# Revit family: Kabelleiter- LG630 VS 3 FS, FT, FT SO
name_source: partatom
category: Generic Models
revit_build: Autodesk Revit 2017 (Build: 20190508_0315(x64)
units: mm (PartAtom-declared; Revit-internal decimal feet)

## family parameters
Always vertical = Yes
Can host rebar = No
Cut with Voids When Loaded = No
Part Type = Normal
Room Calculation Point = No
Round Connector Dimension = Use Diameter
Shared = No
Work Plane-Based = No

## types (3) — shared parameters
Cut's number = 40
Cut's number 2 = 10
Cut's space = 75 mm
Cut's space 2 = 300 mm
Height = 60 mm  [stored 0.19685 ft]
Length = 3000 mm  [stored 9.84252 ft]
Manufacturer = OBO Bettermann
URL = http://obo-bettermann.com
Width = 300 mm
Width/2 = 150 mm

## per-type parameters (varying)
| type | GTIN | Manufacturer Art.No. | Material |
| LG 630 VS 3 FS | 4012195064053 | 6208541 | Strip-galvanised |
| LG 630 VS 3 FT | 4012195434160 | 6208566 | Hot-dip galvanised |
| LG 630 VS 3FT SO | 4012195363279 | 7186361 | Hot-dip galvanised 85 µm |

note: column(s) folded — value = type name in every type: Article Type

note: [stored X ft] marks values corroborated as IEEE doubles in the binary element streams (Revit-internal decimal feet)

## geometry (parser evidence)
native form markers: Sweep x2
no freeform markers — native parametric forms only
